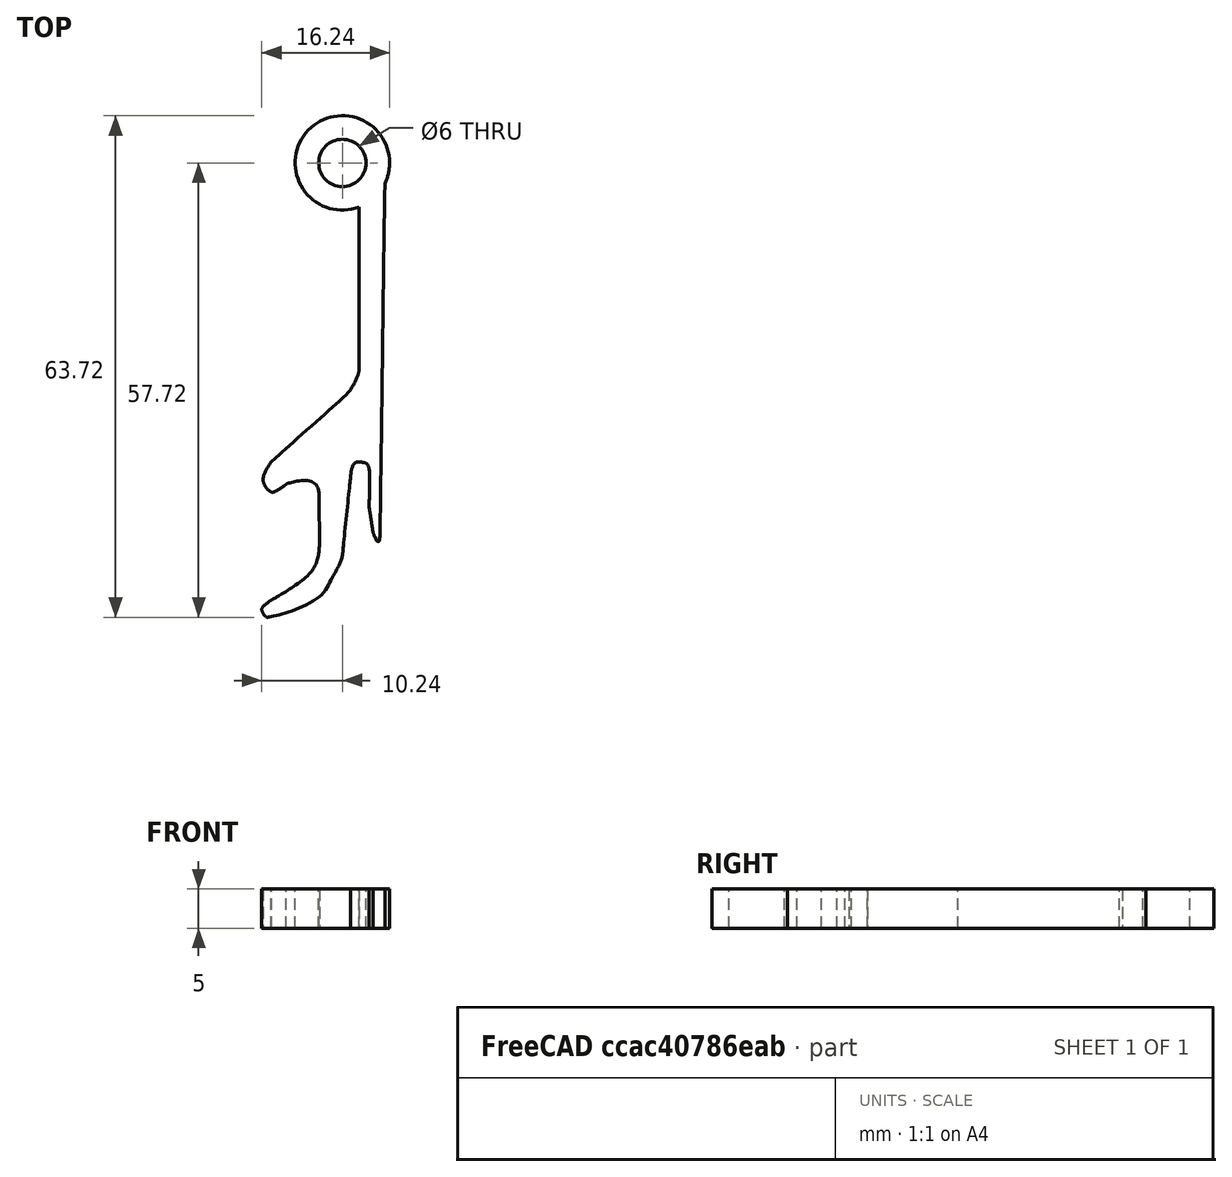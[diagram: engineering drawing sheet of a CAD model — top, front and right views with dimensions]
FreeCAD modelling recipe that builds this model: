
FCSTD DOCUMENT  (FreeCAD 0.18R16117 (Git))
Label: llaveroDestapador
License: All rights reserved
LicenseURL: http://en.wikipedia.org/wiki/All_rights_reserved
objects: Part::Cylinder×2, Sketcher::SketchObject×1, PartDesign::Body×1, Part::Feature×1, Part::Extrusion×1, Part::MultiFuse×1, Part::Cut×1, Mesh::Feature×1
note: 8 computed .brp shape members not serialized (recipe doc carries the construction recipe); baked Part::Feature solids carry a one-line shape summary decoded from their .brp

FEATURE [Sketcher::SketchObject] Sketch
  MapMode = 5
  Support = -> [XY_Plane]
  sketch-geometry (4):
    g0: LineSegment StartX=-5 StartY=-5 StartZ=0 EndX=5 EndY=-5 EndZ=0
    g1: LineSegment StartX=5 StartY=-5 StartZ=0 EndX=5 EndY=5 EndZ=0
    g2: LineSegment StartX=5 StartY=5 StartZ=0 EndX=-5 EndY=5 EndZ=0
    g3: LineSegment StartX=-5 StartY=5 StartZ=0 EndX=-5 EndY=-5 EndZ=0
  constraints (8):
    c: Coincident(g0,g1)
    c: Coincident(g1,g2)
    c: Coincident(g2,g3)
    c: Coincident(g3,g0)
    c: Horizontal(g0)
    c: Horizontal(g2)
    c: Vertical(g1)
    c: Vertical(g3)
FEATURE [PartDesign::Body] Body
  Group = -> [Sketch]
  Origin = -> Origin
FEATURE [Part::Feature] path4564
  shape: bbox 15.73 x 62.95 x 2e-07 mm, 0 faces, 0 solids (baked)
FEATURE [Part::Extrusion] Extrude
  Base = -> path4564
  Dir = (0,0,1)
  DirMode = 0
  FaceMakerClass = Part::FaceMakerBullseye
  LengthFwd = 5
  LengthRev = 0
  Solid = true
  Symmetric = false
FEATURE [Part::Cylinder] Cylinder  label="Cilindro"
  Angle = 360
  AttacherType = Attacher::AttachEngine3D
  Height = 5
  Placement = pos=(-2,18,0) rot=(0,0,1;0rad)
  Radius = 6
FEATURE [Part::MultiFuse] Fusion
  Refine = true
  Shapes = -> [Cylinder,Extrude]
FEATURE [Part::Cylinder] Cylinder001  label="Cilindro001"
  Angle = 360
  AttacherType = Attacher::AttachEngine3D
  Height = 10
  Placement = pos=(-2,18,0) rot=(0,0,1;0rad)
  Radius = 3
FEATURE [Part::Cut] Cut  label="bottleOpener_keyChain"
  Base = -> Fusion
  Refine = true
  Tool = -> Cylinder001
FEATURE [Mesh::Feature] llave
  Placement = pos=(-2,1,0) rot=(0,0,1;0rad)
